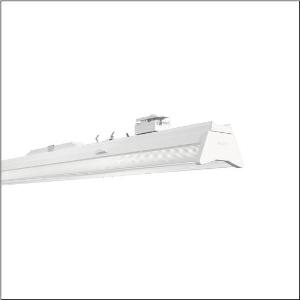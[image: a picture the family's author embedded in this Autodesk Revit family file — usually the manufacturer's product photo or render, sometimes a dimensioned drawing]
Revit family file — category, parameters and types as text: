
# Revit family: licross_r__21_performance_mo_52tm167n485g_c234
name_source: partatom
category: Lighting Fixtures
units: mm (PartAtom-declared; Revit-internal decimal feet)

## family parameters
Cut with Voids When Loaded = No
Host = Face
Light Source = No
Part Type = Normal
Room Calculation Point = No
Round Connector Dimension = Use Diameter
Shared = No

## types (1)
- Licross® 21 Performance MO (1 x LED, 8720 lm, 47.9 W, 4000K)
    Apparent Load = 48 VA
    CIE Flux Codes = 66 88 96 79 100
    Color Rendering = 80
    Color Temperature = 4000K
    Default Elevation = 1800 mm
    Description = Licross® 21 Performance MO, luminaire insert, of sheet steel, galvanised, coil coated, white, length: 1.500mm, width: 120mm, height: 123mm, LED rated luminous flux: 8.720lm, light colour: 840, control gear: ON/OFF, with plug, 3-pole, with phase selection, mains connection: 220..240V, AC, 50/60Hz, rated input power: 48W, halogen-free wiring, primary light control with lens, of plastic, primary optical cover: cover, of PMMA, light emission: direct/indirect distribution, primary light characteristic: symmetric, protection rating (complete): IP40, insulation class (complete): insulation class I (protective earthing), certification: CE, ENEC, UKCA, protection symbol: D if used in an environment without relevant dust loads with corresponding accessories, impact resistance: IK06, permissible ambient temperature for indoor applications: -35..+45°C, corresponds to IFS (International Featured Standards) requirements for safety and quality in the food industry, reducing of maximum allowable ambient temperature of 5°C with ceiling mounting, LABS conformity tested according to VDMA 24364:2018-05, packaging unit: 1 piece
    Height = 114 mm
    Lamp = 1 x LED
    Lamp Light Flux = 8720 lm
    Lamp Power = 47.9 W
    Lamp count = 1
    Length = 1500 mm
    Luminous efficacy = 182 lm/W
    Manufacturer = Siteco
    ModVariant = No
    Model = 52TM167N485G
    Mounting Place = Ceiling
    Mounting Type = Pendant
    Number of Poles = 1
    OnlyDefault = Yes
    Power Factor = 1
    Product Name = Licross® 21 Performance MO
    Product group = luminaire insert
    ProductGroupID = 901
    Protection Class = Protection class I
    Protection Degree = IP 40
    RLX_Detail_Level = 1
    RLX_Emergency_Light_Flux = 0 lm
    RLX_Emergency_Type = 0
    RLX_Emergency_Type_DB = No
    RlxData = <blob elided: 30429 chars, md5=a0181a9c>
    Socket = socket
    Standby Power = 0 W
    System Light Flux = 8720 lm
    System Power = 48 W
    Type Comments = Product without accessories
    Type Image = l_1256138.jpg
    URL = http://relux.com
    VarID = ---
    Voltage = 0 V
    Weight = 0.00 kg
    Width = 120 mm

## geometry (parser evidence)
native form markers: Blend x4, Sweep x13
no freeform markers — native parametric forms only
